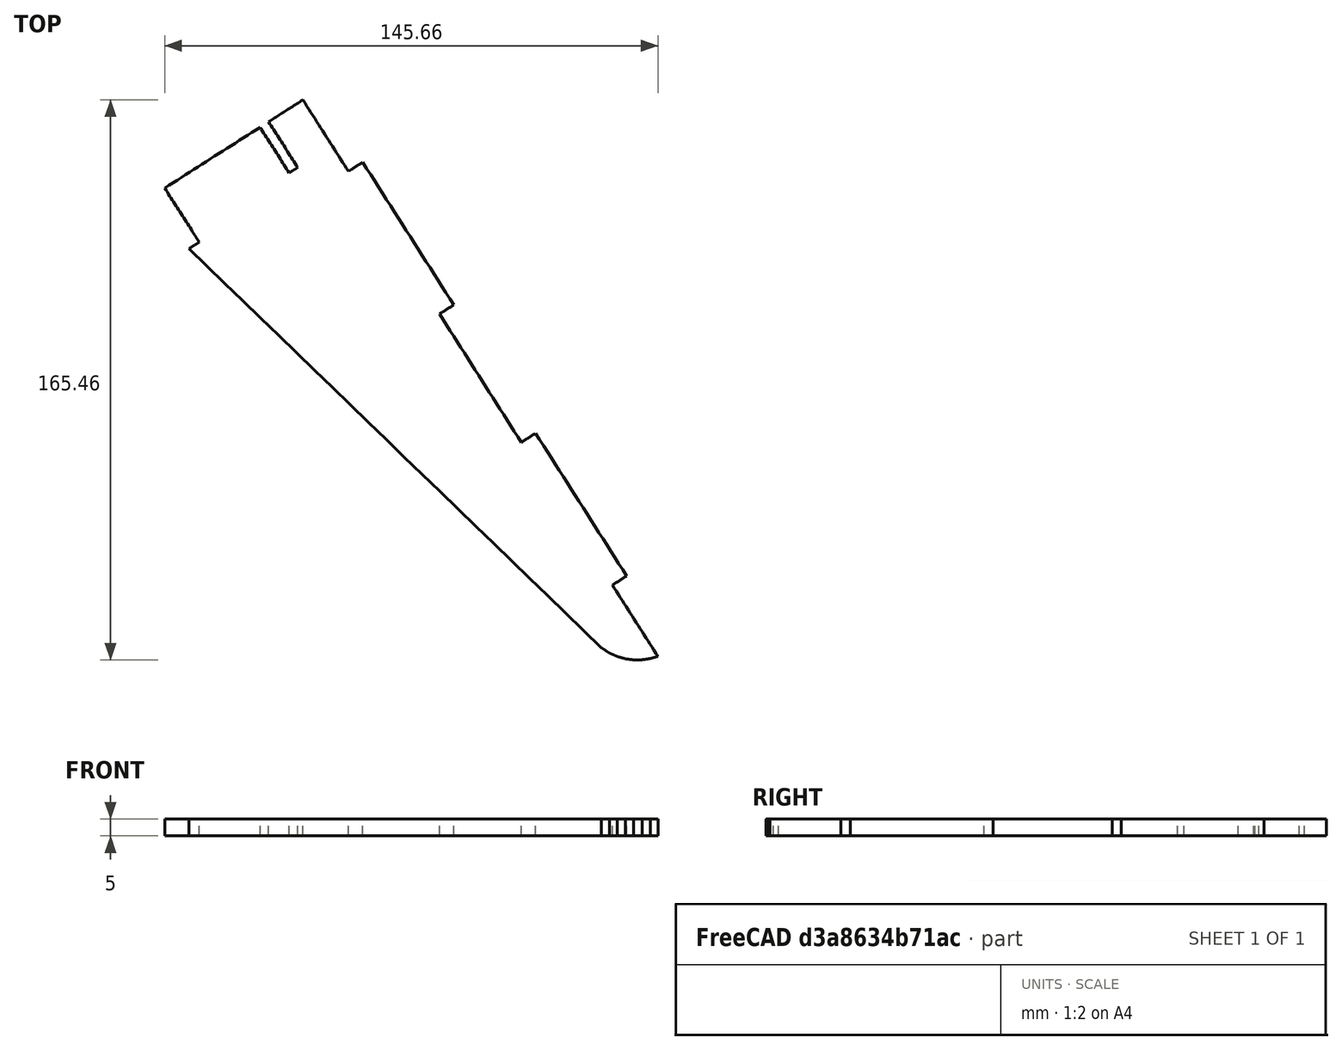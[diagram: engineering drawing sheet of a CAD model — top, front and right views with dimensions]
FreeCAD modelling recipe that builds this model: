
FCSTD DOCUMENT  (FreeCAD 0.19R)
Label: F-35_v2_parts_12
License: All rights reserved
LicenseURL: http://en.wikipedia.org/wiki/All_rights_reserved
objects: App::DocumentObjectGroup×2, PartDesign::CoordinateSystem×2, App::FeaturePython×1, Sketcher::SketchObject×1, PartDesign::Pad×1, PartDesign::Body×1, App::Part×1
note: 6 computed .brp shape members not serialized (recipe doc carries the construction recipe); baked Part::Feature solids carry a one-line shape summary decoded from their .brp

FEATURE [App::DocumentObjectGroup] Parts
FEATURE [PartDesign::CoordinateSystem] LCS_Origin
  AttacherType = Attacher::AttachEngine3D
  MapMode = 2
  Support = -> [X_Axis]
FEATURE [App::DocumentObjectGroup] Constraints
FEATURE [App::FeaturePython] Variables  # WARN: FeaturePython — macro-defined, semantics opaque (R4)
FEATURE [Sketcher::SketchObject] Sketch011
  FullyConstrained = false
  sketch-geometry (25):
    g0: BSplineCurve PolesCount=2 KnotsCount=2 Degree=1 IsPeriodic=0
    g1: BSplineCurve PolesCount=2 KnotsCount=2 Degree=1 IsPeriodic=0
    g2: BSplineCurve PolesCount=2 KnotsCount=2 Degree=1 IsPeriodic=0
    g3: BSplineCurve PolesCount=2 KnotsCount=2 Degree=1 IsPeriodic=0
    g4: BSplineCurve PolesCount=2 KnotsCount=2 Degree=1 IsPeriodic=0
    g5: BSplineCurve PolesCount=2 KnotsCount=2 Degree=1 IsPeriodic=0
    g6: BSplineCurve PolesCount=2 KnotsCount=2 Degree=1 IsPeriodic=0
    g7: BSplineCurve PolesCount=2 KnotsCount=2 Degree=1 IsPeriodic=0
    g8: BSplineCurve PolesCount=2 KnotsCount=2 Degree=1 IsPeriodic=0
    g9: BSplineCurve PolesCount=2 KnotsCount=2 Degree=1 IsPeriodic=0
    g10: BSplineCurve PolesCount=2 KnotsCount=2 Degree=1 IsPeriodic=0
    g11: BSplineCurve PolesCount=2 KnotsCount=2 Degree=1 IsPeriodic=0
    g12: BSplineCurve PolesCount=2 KnotsCount=2 Degree=1 IsPeriodic=0
    g13: BSplineCurve PolesCount=2 KnotsCount=2 Degree=1 IsPeriodic=0
    g14: BSplineCurve PolesCount=2 KnotsCount=2 Degree=1 IsPeriodic=0
    g15: BSplineCurve PolesCount=2 KnotsCount=2 Degree=1 IsPeriodic=0
    g16: BSplineCurve PolesCount=2 KnotsCount=2 Degree=1 IsPeriodic=0
    g17: BSplineCurve PolesCount=2 KnotsCount=2 Degree=1 IsPeriodic=0
    g18: BSplineCurve PolesCount=2 KnotsCount=2 Degree=1 IsPeriodic=0
    g19: BSplineCurve PolesCount=2 KnotsCount=2 Degree=1 IsPeriodic=0
    g20: BSplineCurve PolesCount=2 KnotsCount=2 Degree=1 IsPeriodic=0
    g21: BSplineCurve PolesCount=2 KnotsCount=2 Degree=1 IsPeriodic=0
    g22: BSplineCurve PolesCount=2 KnotsCount=2 Degree=1 IsPeriodic=0
    g23: BSplineCurve PolesCount=2 KnotsCount=2 Degree=1 IsPeriodic=0
    g24: BSplineCurve PolesCount=2 KnotsCount=2 Degree=1 IsPeriodic=0
  constraints (6):
    c: Coincident(g14,g15)
    c: Coincident(g15,g16)
    c: Coincident(g16,g17)
    c: Coincident(g17,g18)
    c: Coincident(g18,g19)
    c: Coincident(g19,g20)
FEATURE [PartDesign::Pad] Pad010
  Direction = (1,1,1)
  Length = 5
  Length2 = 100
  Profile = -> Sketch011
  Type = 0
FEATURE [PartDesign::Body] Body011  label="Part12"
  Group = -> [Sketch011,Pad010]
  Origin = -> Origin012
  Tip = -> Pad010
FEATURE [PartDesign::CoordinateSystem] LCS_1
  AttacherType = Attacher::AttachEngine3D
  AttachmentOffset = pos=(0,0,0) rot=(0,0,1;1.01229rad)
  MapMode = 7
  Placement = pos=(528.368,-249.96,0) rot=(0.48481,0.87462,0;3.14159rad)
  Support = -> [Pad010]
FEATURE [App::Part] Model
  Configuration = 0
  Group = -> [LCS_Origin,Constraints,Variables,Body011,LCS_1]
  Origin = -> Origin
  Type = Assembly4 Model
